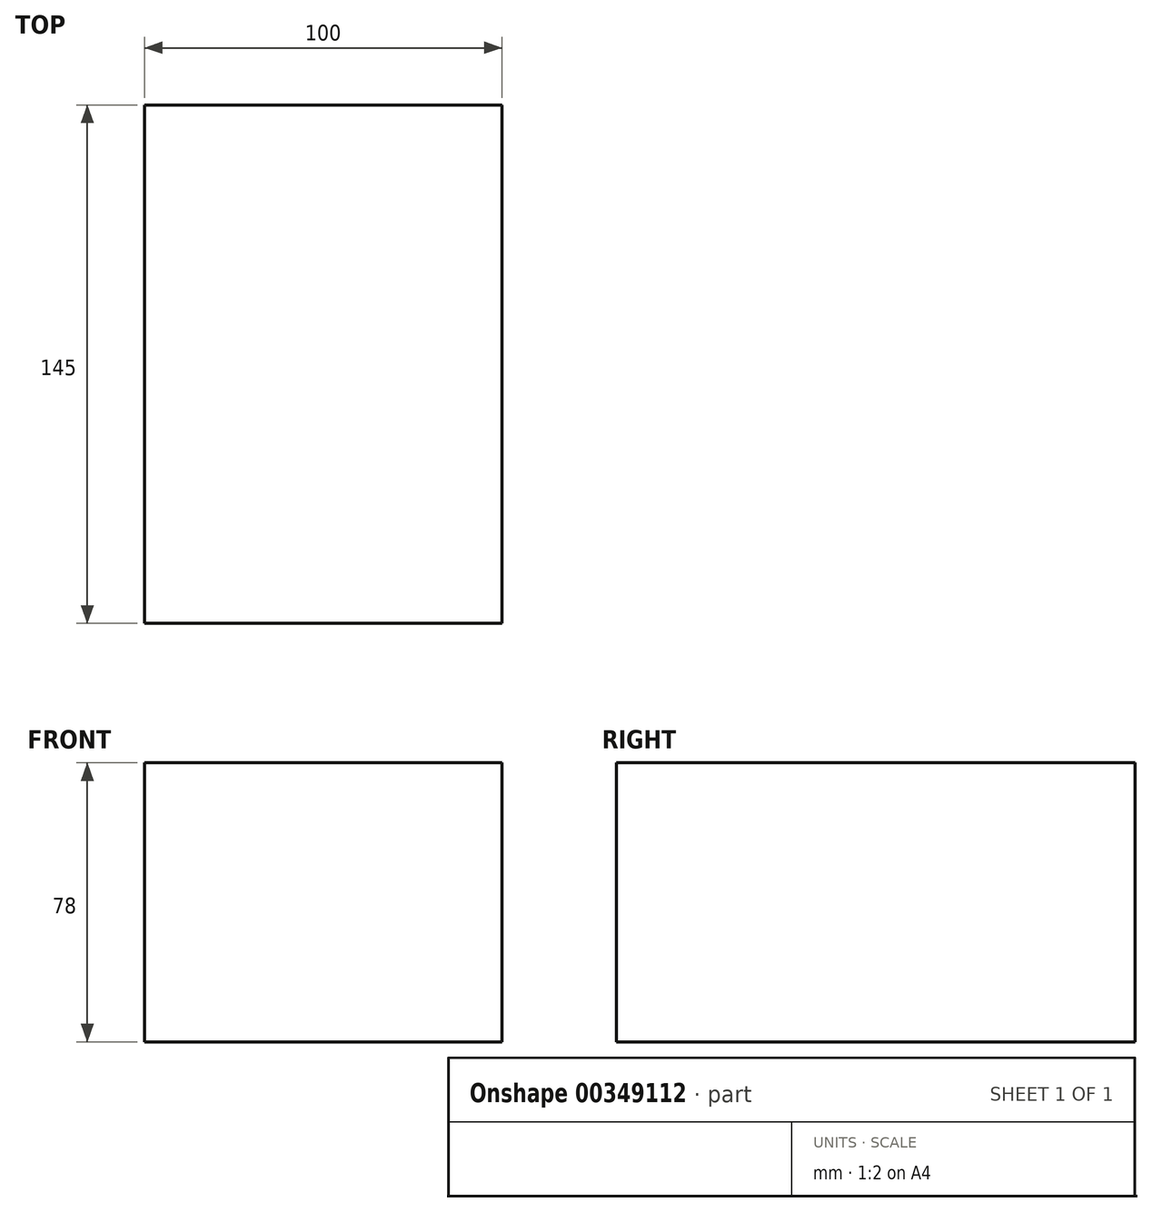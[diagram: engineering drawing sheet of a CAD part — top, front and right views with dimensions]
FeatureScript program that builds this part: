
annotation { "Feature Type Name" : "Feature", "Feature Type Description" : "" }
export const myFeature = defineFeature(function(context is Context, id is Id, definition is map)
    precondition{}
    {
        {
            var Q0;
            Q0=qCreatedBy(makeId("Top.planeOp"),FACE);
            var sketch = newSketch(context, id + "F0", { "sketchPlane" : qUnion([Q0])});
            skLineSegment(sketch, "E0.bottom", {"start": v(-50, 72.5) * mm, "end": v(50, 72.5) * mm});
            skLineSegment(sketch, "E0.top", {"start": v(-50, -72.5) * mm, "end": v(50, -72.5) * mm});
            skLineSegment(sketch, "E0.left", {"start": v(-50, 72.5) * mm, "end": v(-50, -72.5) * mm});
            skLineSegment(sketch, "E0.right", {"start": v(50, 72.5) * mm, "end": v(50, -72.5) * mm});
            skSolve(sketch);
        }
        {
            var Q0;
            Q0 = qSketchRegion(id + "F0", true);
            extrude(context, id + "F1", {"entities" : qUnion([Q0]), "endBound" : BoundingType.SYMMETRIC, "depth" : 78 * mm});
        }
    });
